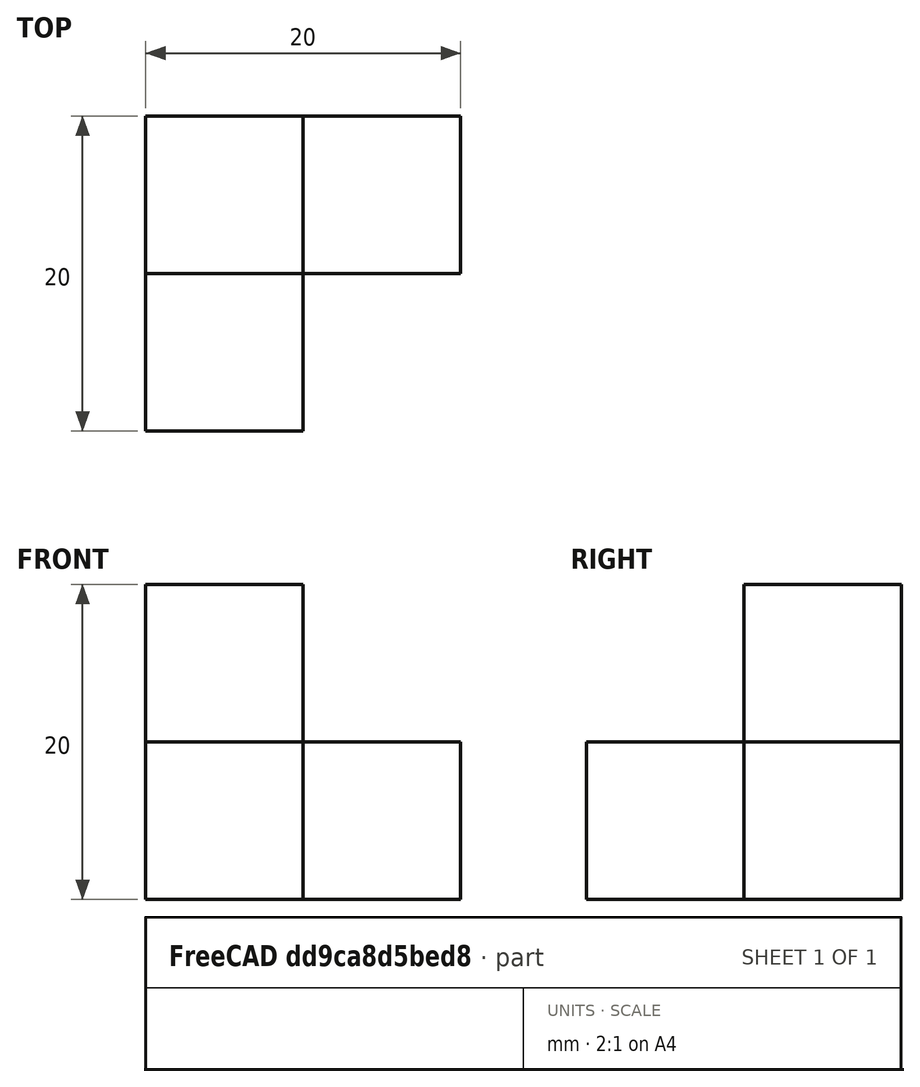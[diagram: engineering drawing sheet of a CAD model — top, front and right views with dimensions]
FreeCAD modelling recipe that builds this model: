
FCSTD DOCUMENT  (FreeCAD 0.21R33694 (Git))
Label: OJT1_T04P01_qbert2nivells
License: All rights reserved
LicenseURL: https://en.wikipedia.org/wiki/All_rights_reserved
objects: Part::Box×4
note: 4 computed .brp shape members not serialized (recipe doc carries the construction recipe); baked Part::Feature solids carry a one-line shape summary decoded from their .brp

FEATURE [Part::Box] Box  label="Cub1_nivell1"
  AttacherType = Attacher::AttachEngine3D
  Height = 10
  Length = 10
  Width = 10
FEATURE [Part::Box] Box001  label="Cub2_nivell1"
  AttacherType = Attacher::AttachEngine3D
  Height = 10
  Length = 10
  Placement = pos=(10,0,0) rot=(0,0,1;0rad)
  Width = 10
FEATURE [Part::Box] Box002  label="Cub3_nivell1"
  AttacherType = Attacher::AttachEngine3D
  Height = 10
  Length = 10
  Placement = pos=(0,-10,0) rot=(0,0,1;0rad)
  Width = 10
FEATURE [Part::Box] Box003  label="Cub1_nivell2"
  AttacherType = Attacher::AttachEngine3D
  Height = 10
  Length = 10
  Placement = pos=(0,0,10) rot=(0,0,1;0rad)
  Width = 10
